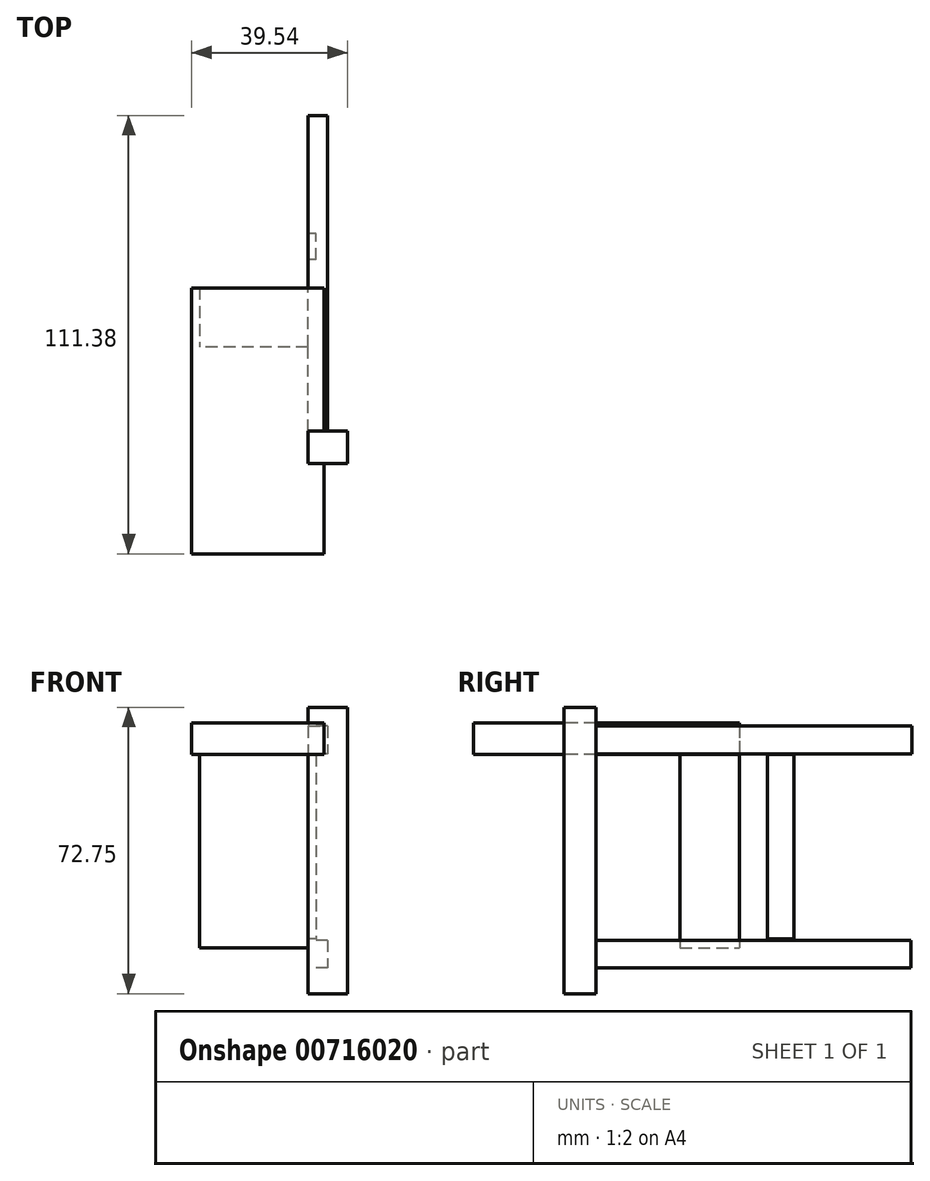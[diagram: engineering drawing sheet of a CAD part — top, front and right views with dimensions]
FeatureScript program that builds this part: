
annotation { "Feature Type Name" : "Feature", "Feature Type Description" : "" }
export const myFeature = defineFeature(function(context is Context, id is Id, definition is map)
    precondition{}
    {
        {
            var Q0;
            Q0=qCreatedBy(makeId("Right.planeOp"),FACE);
            var sketch = newSketch(context, id + "F0", { "sketchPlane" : qUnion([Q0])});
            skLineSegment(sketch, "E0.bottom", {"start": v(-44.59, 37.9) * mm, "end": v(-36.38, 37.9) * mm});
            skLineSegment(sketch, "E0.top", {"start": v(-44.59, -34.85) * mm, "end": v(-36.38, -34.85) * mm});
            skLineSegment(sketch, "E0.left", {"start": v(-44.59, 37.9) * mm, "end": v(-44.59, -34.85) * mm});
            skLineSegment(sketch, "E0.right", {"start": v(-36.38, 37.9) * mm, "end": v(-36.38, -34.85) * mm});
            skSolve(sketch);
        }
        {
            var Q0;
            Q0=makeQuery(id+"F0.imprint","IMPRINT",FACE,{"disambiguationData":[TD([[makeQuery(id+"F0.imprint","IMPRINT",EDGE,{"derivedFrom":sQuery(id+"F0.wireOp",EDGE,"E0.bottom")}),-1.0]])]});
            extrude(context, id + "F1", {"entities" : qUnion([Q0]), "depth" : 10 * mm, "offsetDistance" : 25.4 * mm});
        }
        {
            var Q0;
            Q0=qCreatedBy(makeId("Right.planeOp"),FACE);
            var sketch = newSketch(context, id + "F2", { "sketchPlane" : qUnion([Q0])});
            skLineSegment(sketch, "E1.bottom", {"start": v(-36.38, 33.13) * mm, "end": v(43.82, 33.13) * mm});
            skLineSegment(sketch, "E1.top", {"start": v(-36.38, 26.07) * mm, "end": v(43.82, 26.07) * mm});
            skLineSegment(sketch, "E1.left", {"start": v(-36.38, 33.13) * mm, "end": v(-36.38, 26.07) * mm});
            skLineSegment(sketch, "E1.right", {"start": v(43.82, 33.13) * mm, "end": v(43.82, 26.07) * mm});
            skSolve(sketch);
        }
        {
            var Q0;
            Q0=makeQuery(id+"F2.imprint","IMPRINT",FACE,{"disambiguationData":[TD([[makeQuery(id+"F2.imprint","IMPRINT",EDGE,{"derivedFrom":sQuery(id+"F2.wireOp",EDGE,"E1.bottom")}),-1.0]])]});
            extrude(context, id + "F3", {"entities" : qUnion([Q0]), "operationType" : NewBodyOperationType.ADD, "depth" : 5 * mm, "offsetDistance" : 25.4 * mm});
        }
        {
            var Q0;
            Q0=qCreatedBy(makeId("Right.planeOp"),FACE);
            var sketch = newSketch(context, id + "F4", { "sketchPlane" : qUnion([Q0])});
            skLineSegment(sketch, "E2.bottom", {"start": v(-36.38, -21.3) * mm, "end": v(43.63, -21.3) * mm});
            skLineSegment(sketch, "E2.top", {"start": v(-36.38, -28.36) * mm, "end": v(43.63, -28.36) * mm});
            skLineSegment(sketch, "E2.left", {"start": v(-36.38, -21.3) * mm, "end": v(-36.38, -28.36) * mm});
            skLineSegment(sketch, "E2.right", {"start": v(43.63, -21.3) * mm, "end": v(43.63, -28.36) * mm});
            skSolve(sketch);
        }
        {
            var Q0;
            Q0=makeQuery(id+"F4.imprint","IMPRINT",FACE,{"disambiguationData":[TD([[makeQuery(id+"F4.imprint","IMPRINT",EDGE,{"derivedFrom":sQuery(id+"F4.wireOp",EDGE,"E2.bottom")}),-1.0]])]});
            extrude(context, id + "F5", {"entities" : qUnion([Q0]), "operationType" : NewBodyOperationType.ADD, "depth" : 5 * mm, "offsetDistance" : 25.4 * mm});
        }
        {
            var Q0;
            Q0=qCreatedBy(makeId("Right.planeOp"),FACE);
            var sketch = newSketch(context, id + "F6", { "sketchPlane" : qUnion([Q0])});
            skArc(sketch, "E3", {"start": v(7.35, 25.87) * mm, "mid": v(3.44, 0.86) * mm, "end": v(7.35, -24.16) * mm});
            skSolve(sketch);
        }
        {
            var Q0;
            Q0=qCreatedBy(makeId("Right.planeOp"),FACE);
            var sketch = newSketch(context, id + "F7", { "sketchPlane" : qUnion([Q0])});
            skLineSegment(sketch, "E4.bottom", {"start": v(7.16, 25.87) * mm, "end": v(13.84, 25.87) * mm});
            skLineSegment(sketch, "E4.top", {"start": v(7.16, -20.9) * mm, "end": v(13.84, -20.9) * mm});
            skLineSegment(sketch, "E4.left", {"start": v(7.16, 25.87) * mm, "end": v(7.16, -20.9) * mm});
            skLineSegment(sketch, "E4.right", {"start": v(13.84, 25.87) * mm, "end": v(13.84, -20.9) * mm});
            skSolve(sketch);
        }
        {
            var Q0;
            Q0=makeQuery(id+"F7.imprint","IMPRINT",FACE,{"disambiguationData":[TD([[makeQuery(id+"F7.imprint","IMPRINT",EDGE,{"derivedFrom":sQuery(id+"F7.wireOp",EDGE,"E4.bottom")}),-1.0]])]});
            extrude(context, id + "F8", {"entities" : qUnion([Q0]), "depth" : 2 * mm, "offsetDistance" : 25.4 * mm});
        }
        {
            var Q0;
            Q0=qCreatedBy(makeId("Front.planeOp"),FACE);
            var sketch = newSketch(context, id + "F9", { "sketchPlane" : qUnion([Q0])});
            skLineSegment(sketch, "E5.bottom", {"start": v(0, 26.9) * mm, "end": v(-27.5, 26.9) * mm});
            skLineSegment(sketch, "E5.top", {"start": v(0, -23.16) * mm, "end": v(-27.5, -23.16) * mm});
            skLineSegment(sketch, "E5.left", {"start": v(0, 26.9) * mm, "end": v(0, -23.16) * mm});
            skLineSegment(sketch, "E5.right", {"start": v(-27.5, 26.9) * mm, "end": v(-27.5, -23.16) * mm});
            skSolve(sketch);
        }
        {
            var Q0;
            Q0=makeQuery(id+"F9.imprint","IMPRINT",FACE,{"disambiguationData":[TD([[makeQuery(id+"F9.imprint","IMPRINT",EDGE,{"derivedFrom":sQuery(id+"F9.wireOp",EDGE,"E5.bottom")}),1.0]])]});
            extrude(context, id + "F10", {"entities" : qUnion([Q0]), "operationType" : NewBodyOperationType.ADD, "depth" : 15 * mm, "offsetDistance" : 25.4 * mm});
        }
        {
            var Q0;
            Q0=qCreatedBy(makeId("Front.planeOp"),FACE);
            var sketch = newSketch(context, id + "F11", { "sketchPlane" : qUnion([Q0])});
            skLineSegment(sketch, "E6.bottom", {"start": v(-29.54, 33.97) * mm, "end": v(4.07, 33.97) * mm});
            skLineSegment(sketch, "E6.top", {"start": v(-29.54, 25.88) * mm, "end": v(4.07, 25.88) * mm});
            skLineSegment(sketch, "E6.left", {"start": v(-29.54, 33.97) * mm, "end": v(-29.54, 25.88) * mm});
            skLineSegment(sketch, "E6.right", {"start": v(4.07, 33.97) * mm, "end": v(4.07, 25.88) * mm});
            skSolve(sketch);
        }
        {
            var Q0;
            Q0=makeQuery(id+"F11.imprint","IMPRINT",FACE,{"disambiguationData":[TD([[makeQuery(id+"F11.imprint","IMPRINT",EDGE,{"derivedFrom":sQuery(id+"F11.wireOp",EDGE,"E6.bottom")}),-1.0]])]});
            extrude(context, id + "F12", {"entities" : qUnion([Q0]), "operationType" : NewBodyOperationType.ADD, "depth" : 67.56 * mm, "offsetDistance" : 25.4 * mm});
        }
    });
